# Revit family: Electronics_Desono_Biamp_Two-Way-High-Efficiency-Loudspeaker_DX-IC10
name_source: partatom
category: Communication Devices
units: mm (PartAtom-declared; Revit-internal decimal feet)

## family parameters
Cut with Voids When Loaded = No
Host = Face
Maintain Annotation Orientation = No
OmniClass Number = 23.85.10.11.14.14.14
OmniClass Title = Loudspeakers
Part Type = Normal
Room Calculation Point = No
Round Connector Dimension = Use Diameter
Shared = No

## types (1)
- DX-IC10
    Autoformer = 70 V: 200 W, 100 W, 50 W, 25 W; 100 V: 200 W, 100 W, 50 W
    Certifcations = ETL listed to comply with UL1480A, UL2043 and CSA62368-1 Suitable for use in air handling spaces per NFPA 70 and NFPA 90
    Connector Description = 4-way Euroblock; Low impedance 8 ohms, 70/100V operation
    Controls = Front-face wattage / low impedance selector switch
    Crossover Frequency = 1.0 kHz
    Default Elevation = 4' - 0"
    Depth = 0' - 10 1/2"
    Description = Desono™ DX-IC10 Two-Way 10-Inch High Output Ceiling Mount Loudspeaker
    Diameter = 1' - 3 1/2"
    Grill Material = Biamp - Plastic - White(Grid)
    Housing Material = Biamp - Plastic - Black
    Input Connection = 4-position Euroblock connector
    Manufacturer = Biamp
    Model = DX-IC10
    Mounting Provisions = 4 SpringLock mounting clamps with 2.5-inch grip range
    Nominal Beamwidth (H x V) = 115°, conical
    Nominal Continuous Power = Passive - 39 V; (240 W @ 6.5 Ω)
    Nominal Maximum SPL = Passive: Peak - 125dB; Continuous - 119dB
    Operating Environment = Indoor
    Operating Mode = Passive with DSP
    Operating Range (-10dB) = 65 Hz to 20 kHz
    Product Documentation Link = https://downloads.biamp.com
    Product Page URL = https://www.biamp.com
    Product data url = https://www.bimobject.com
    Rated Continuous Voltage = Passive: 39.8 V; (32 dBV)
    Rated Maximum SPL (Processed) = Passive: Peak - 131dB; Continuous - 119dB
    Recommended Amplifers = Passive: 240 W - 480 W into 8 Ω, (44 V - 62 V)
    Required Accessory = 75 Hz, 12 dB/oct. high pass flter
    Sensitivity = 97 dB (2.83 V); 96 dB (1 W at rated impedance 6.5 Ω)
    Shipping Weight = 58.76 lb
    Transducers = LF 1 x 10 (254 mm); HF 1 x 1.25 (32 mm) exit compression driver
    URL = https://www.biamp.com
    Weight = 23.66 lb

## geometry (parser evidence)
native form markers: Sweep x8
no freeform markers — native parametric forms only
